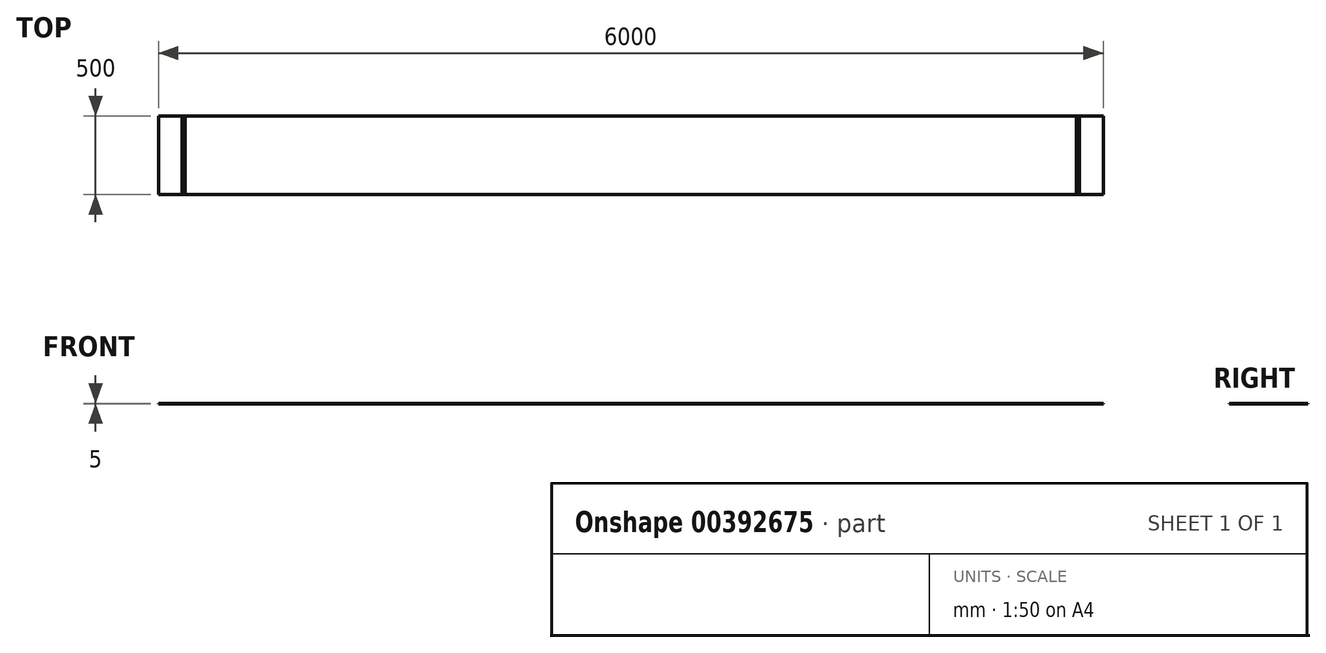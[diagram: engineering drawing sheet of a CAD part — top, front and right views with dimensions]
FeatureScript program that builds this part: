
annotation { "Feature Type Name" : "Feature", "Feature Type Description" : "" }
export const myFeature = defineFeature(function(context is Context, id is Id, definition is map)
    precondition{}
    {
        {
            var Q0;
            Q0=qCreatedBy(makeId("Top.planeOp"),FACE);
            var sketch = newSketch(context, id + "F0", { "sketchPlane" : qUnion([Q0])});
            skLineSegment(sketch, "E0.bottom", {"start": v(-3000, -250) * mm, "end": v(3000, -250) * mm});
            skLineSegment(sketch, "E0.top", {"start": v(-3000, 250) * mm, "end": v(3000, 250) * mm});
            skLineSegment(sketch, "E0.left", {"start": v(-3000, -250) * mm, "end": v(-3000, 250) * mm});
            skLineSegment(sketch, "E0.right", {"start": v(3000, -250) * mm, "end": v(3000, 250) * mm});
            skPoint(sketch, "E0.middle", {"position": v(0, 0) * mm});
            skSolve(sketch);
        }
        {
            var Q0;
            Q0 = qSketchRegion(id + "F0", true);
            extrude(context, id + "F1", {"entities" : qUnion([Q0]), "depth" : 5 * mm});
        }
        {
            var Q0;
            Q0=makeQuery(id+"F1.opExtrude","CAP_FACE",FACE,{"disambiguationData":[OSD([sQuery(id+"F0.wireOp",EDGE,"E0.bottom"),sQuery(id+"F0.wireOp",EDGE,"E0.top"),sQuery(id+"F0.wireOp",EDGE,"E0.left"),sQuery(id+"F0.wireOp",EDGE,"E0.right")])],"isStart":false});
            var sketch = newSketch(context, id + "F2", { "sketchPlane" : qUnion([Q0])});
            skPoint(sketch, "E1.endSnap0", {"position": v(-3000, 0) * mm});
            skPoint(sketch, "E2.endSnap0", {"position": v(3000, 0) * mm});
            skLineSegment(sketch, "E3", {"start": v(-2830, -250) * mm, "end": v(-2830, 250) * mm});
            skLineSegment(sketch, "E4", {"start": v(-2830, 250) * mm, "end": v(-2850, 250) * mm});
            skLineSegment(sketch, "E5", {"start": v(-2850, 250) * mm, "end": v(-2850, -250) * mm});
            skLineSegment(sketch, "E6", {"start": v(-2850, -250) * mm, "end": v(-2830, -250) * mm});
            skLineSegment(sketch, "E7", {"start": v(2850, 0) * mm, "end": v(2850, 250) * mm});
            skLineSegment(sketch, "E8", {"start": v(2850, 250) * mm, "end": v(2830, 250) * mm});
            skLineSegment(sketch, "E9", {"start": v(2830, 250) * mm, "end": v(2830, -250) * mm});
            skLineSegment(sketch, "E10", {"start": v(2830, -250) * mm, "end": v(2850, -250) * mm});
            skLineSegment(sketch, "E11", {"start": v(2850, -250) * mm, "end": v(2850, 0) * mm});
            skSolve(sketch);
        }
        {
            var Q0;
            Q0 = qSketchRegion(id + "F2", true);
            extrude(context, id + "F3", {"entities" : qUnion([Q0]), "operationType" : NewBodyOperationType.REMOVE, "oppositeDirection" : true, "depth" : 2 * mm});
        }
    });
